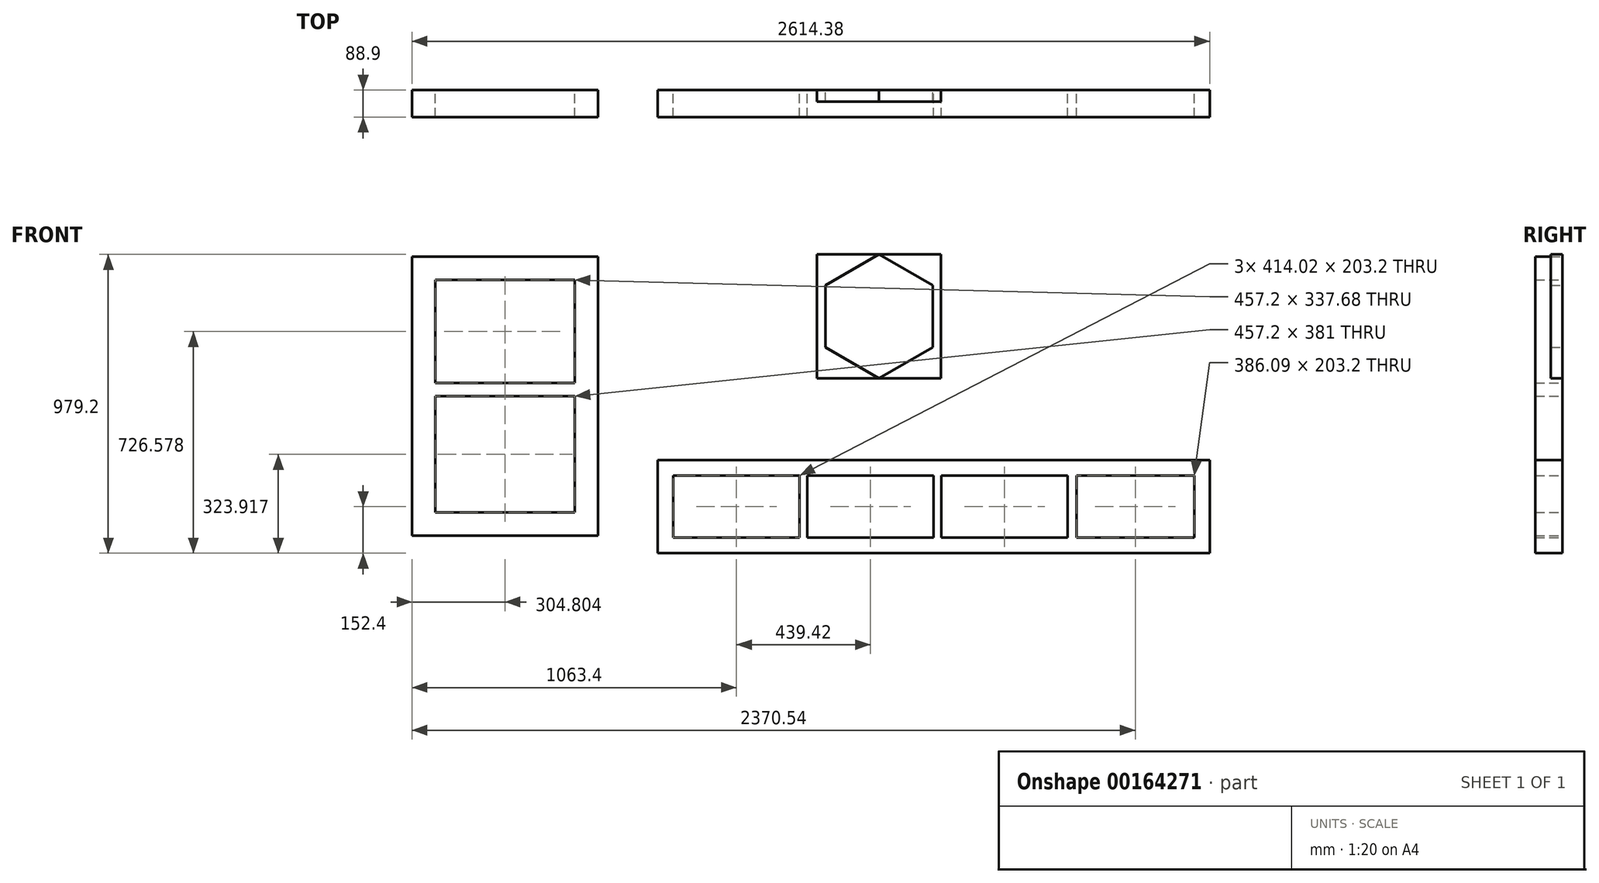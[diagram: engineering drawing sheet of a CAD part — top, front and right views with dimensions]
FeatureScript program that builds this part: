
annotation { "Feature Type Name" : "Feature", "Feature Type Description" : "" }
export const myFeature = defineFeature(function(context is Context, id is Id, definition is map)
    precondition{}
    {
        {
            var Q0;
            Q0=qCreatedBy(makeId("Front.planeOp"),FACE);
            var sketch = newSketch(context, id + "F0", { "sketchPlane" : qUnion([Q0])});
            skLineSegment(sketch, "E0.bottom", {"start": v(-123.06, 304.8) * mm, "end": v(1685.72, 304.8) * mm});
            skLineSegment(sketch, "E0.top", {"start": v(-123.06, 0) * mm, "end": v(1685.72, 0) * mm});
            skLineSegment(sketch, "E0.left", {"start": v(-123.06, 304.8) * mm, "end": v(-123.06, 0) * mm});
            skLineSegment(sketch, "E0.right", {"start": v(1685.72, 304.8) * mm, "end": v(1685.72, 0) * mm});
            skLineSegment(sketch, "E1.0", {"start": v(-123.06, 0.36) * mm, "end": v(1705.74, 0.36) * mm});
            skLineSegment(sketch, "E2.0", {"start": v(-72.26, 254) * mm, "end": v(-72.26, 50.8) * mm});
            skLineSegment(sketch, "E2.1", {"start": v(-72.26, 254) * mm, "end": v(341.76, 254) * mm});
            skLineSegment(sketch, "E2.2", {"start": v(1634.92, 254) * mm, "end": v(1634.92, 50.8) * mm});
            skLineSegment(sketch, "E2.3", {"start": v(-72.26, 50.8) * mm, "end": v(341.76, 50.8) * mm});
            skLineSegment(sketch, "E3.right", {"start": v(341.76, 254) * mm, "end": v(341.76, 50.8) * mm});
            skLineSegment(sketch, "E4.bottom", {"start": v(367.16, 254) * mm, "end": v(781.18, 254) * mm});
            skLineSegment(sketch, "E4.top", {"start": v(367.16, 50.8) * mm, "end": v(781.18, 50.8) * mm});
            skLineSegment(sketch, "E4.left", {"start": v(367.16, 254) * mm, "end": v(367.16, 50.8) * mm});
            skLineSegment(sketch, "E4.right", {"start": v(781.18, 254) * mm, "end": v(781.18, 50.8) * mm});
            skLineSegment(sketch, "E5.bottom", {"start": v(806.58, 254) * mm, "end": v(1220.6, 254) * mm});
            skLineSegment(sketch, "E5.top", {"start": v(806.58, 50.8) * mm, "end": v(1220.6, 50.8) * mm});
            skLineSegment(sketch, "E5.left", {"start": v(806.58, 254) * mm, "end": v(806.58, 50.8) * mm});
            skLineSegment(sketch, "E5.right", {"start": v(1220.6, 254) * mm, "end": v(1220.6, 50.8) * mm});
            skLineSegment(sketch, "E6.bottom", {"start": v(1634.92, 254) * mm, "end": v(1248.84, 254) * mm});
            skLineSegment(sketch, "E6.top", {"start": v(1634.92, 50.8) * mm, "end": v(1248.84, 50.8) * mm});
            skLineSegment(sketch, "E6.right", {"start": v(1248.84, 254) * mm, "end": v(1248.84, 50.8) * mm});
            skLineSegment(sketch, "E7.trimOffspring", {"start": v(1248.84, 254) * mm, "end": v(1634.92, 254) * mm});
            skLineSegment(sketch, "E8.trimOffspring", {"start": v(1248.84, 50.8) * mm, "end": v(1634.92, 50.8) * mm});
            skSolve(sketch);
        }
        {
            var Q0;
            {var subQ0=sQuery(id+"F0.wireOp",EDGE,"E0.top");Q0=makeQuery(id+"F0.imprint","IMPRINT",FACE,{"disambiguationData":[TD([[makeQuery(id+"F0.imprint","IMPRINT",EDGE,{"derivedFrom":subQ0}),1.0]])]});}
            var Q1;
            {var subQ0=sQuery(id+"F0.wireOp",EDGE,"E0.bottom");Q1=makeQuery(id+"F0.imprint","IMPRINT",FACE,{"disambiguationData":[TD([[makeQuery(id+"F0.imprint","IMPRINT",EDGE,{"derivedFrom":subQ0}),-1.0]])]});}
            extrude(context, id + "F1", {"entities" : qUnion([Q0, Q1]), "depth" : 88.9 * mm});
        }
        {
            var Q0;
            Q0=qCreatedBy(makeId("Front.planeOp"),FACE);
            var sketch = newSketch(context, id + "F2", { "sketchPlane" : qUnion([Q0])});
            skLineSegment(sketch, "E9.bottom", {"start": v(-928.66, 971.62) * mm, "end": v(-319.06, 971.62) * mm});
            skLineSegment(sketch, "E9.top", {"start": v(-928.66, 57.22) * mm, "end": v(-319.06, 57.22) * mm});
            skLineSegment(sketch, "E9.left", {"start": v(-928.66, 971.62) * mm, "end": v(-928.66, 57.22) * mm});
            skLineSegment(sketch, "E9.right", {"start": v(-319.06, 971.62) * mm, "end": v(-319.06, 57.22) * mm});
            skLineSegment(sketch, "E10.0", {"start": v(-852.46, 133.42) * mm, "end": v(-395.26, 133.42) * mm});
            skLineSegment(sketch, "E11.0", {"start": v(-395.26, 895.42) * mm, "end": v(-395.26, 557.74) * mm});
            skLineSegment(sketch, "E12.0", {"start": v(-852.46, 895.42) * mm, "end": v(-395.26, 895.42) * mm});
            skLineSegment(sketch, "E13.0", {"start": v(-852.46, 895.42) * mm, "end": v(-852.46, 557.74) * mm});
            skLineSegment(sketch, "E14.bottom", {"start": v(-852.46, 514.42) * mm, "end": v(-395.26, 514.42) * mm});
            skLineSegment(sketch, "E14.top", {"start": v(-852.46, 557.74) * mm, "end": v(-395.26, 557.74) * mm});
            skPoint(sketch, "E15.orphan", {"position": v(-852.46, 971.62) * mm});
            skLineSegment(sketch, "E16.trimOffspring", {"start": v(-852.46, 514.42) * mm, "end": v(-852.46, 133.42) * mm});
            skLineSegment(sketch, "E17.trimOffspring", {"start": v(-395.26, 514.42) * mm, "end": v(-395.26, 133.42) * mm});
            skPoint(sketch, "E18.orphan", {"position": v(-852.46, 57.22) * mm});
            skSolve(sketch);
        }
        {
            var Q0;
            Q0=makeQuery(id+"F2.imprint","IMPRINT",FACE,{"disambiguationData":[TD([[makeQuery(id+"F2.imprint","IMPRINT",EDGE,{"derivedFrom":sQuery(id+"F2.wireOp",EDGE,"E9.bottom")}),-1.0]])]});
            extrude(context, id + "F3", {"entities" : qUnion([Q0]), "depth" : 88.9 * mm});
        }
        {
            var Q0;
            Q0=qCreatedBy(makeId("Front.planeOp"),FACE);
            var sketch = newSketch(context, id + "F4", { "sketchPlane" : qUnion([Q0])});
            skLineSegment(sketch, "E19.bottom", {"start": v(398.6, 979.2) * mm, "end": v(805, 979.2) * mm});
            skLineSegment(sketch, "E19.top", {"start": v(398.6, 572.8) * mm, "end": v(805, 572.8) * mm});
            skLineSegment(sketch, "E19.left", {"start": v(398.6, 979.2) * mm, "end": v(398.6, 572.8) * mm});
            skLineSegment(sketch, "E19.right", {"start": v(805, 979.2) * mm, "end": v(805, 572.8) * mm});
            skLineSegment(sketch, "E20.0", {"start": v(601.8, 979.2) * mm, "end": v(777.79, 877.6) * mm});
            skLineSegment(sketch, "E20.1", {"start": v(777.79, 877.6) * mm, "end": v(777.79, 674.4) * mm});
            skLineSegment(sketch, "E20.2", {"start": v(777.79, 674.4) * mm, "end": v(601.8, 572.8) * mm});
            skLineSegment(sketch, "E20.3", {"start": v(601.8, 572.8) * mm, "end": v(425.83, 674.4) * mm});
            skLineSegment(sketch, "E20.4", {"start": v(425.83, 674.4) * mm, "end": v(425.83, 877.6) * mm});
            skLineSegment(sketch, "E20.5", {"start": v(425.83, 877.6) * mm, "end": v(601.8, 979.2) * mm});
            skSolve(sketch);
        }
        {
            var Q0;
            {var subQ1=sQuery(id+"F4.wireOp",EDGE,"E19.right");Q0=makeQuery(id+"F4.imprint","IMPRINT",FACE,{"disambiguationData":[TD([[makeQuery(id+"F4.imprint","IMPRINT",EDGE,{"derivedFrom":subQ1}),-1.0]])]});}
            var Q1;
            {var subQ1=sQuery(id+"F4.wireOp",EDGE,"E19.left");Q1=makeQuery(id+"F4.imprint","IMPRINT",FACE,{"disambiguationData":[TD([[makeQuery(id+"F4.imprint","IMPRINT",EDGE,{"derivedFrom":subQ1}),1.0]])]});}
            extrude(context, id + "F5", {"entities" : qUnion([Q0, Q1]), "depth" : 38.1 * mm});
        }
    });
